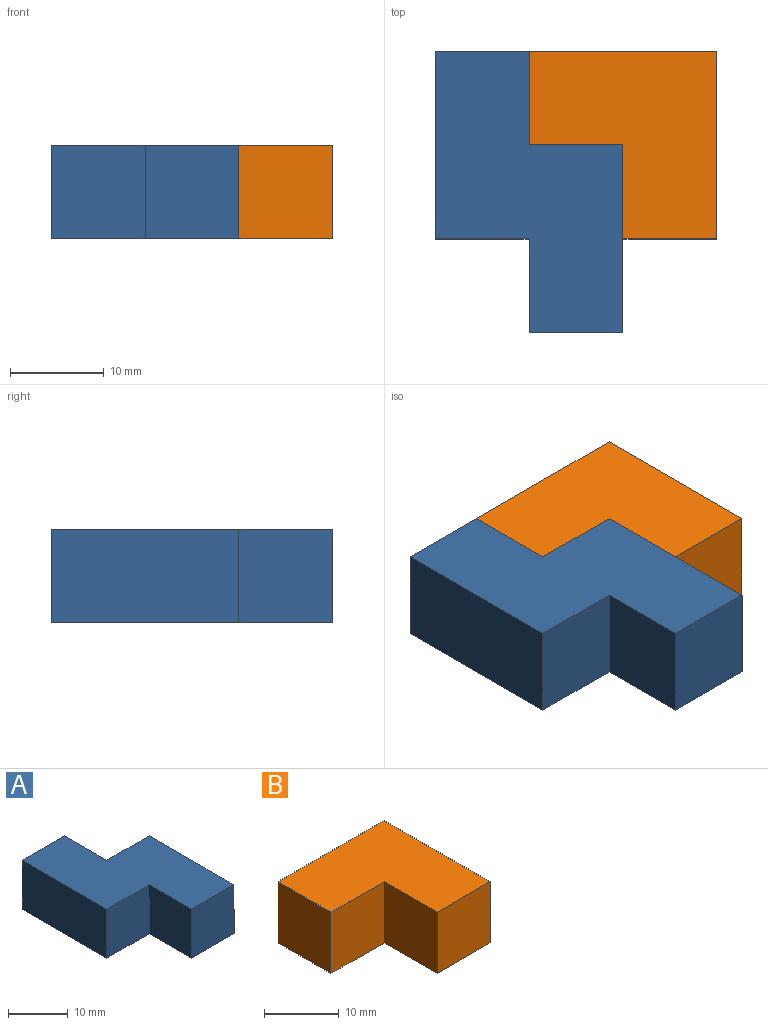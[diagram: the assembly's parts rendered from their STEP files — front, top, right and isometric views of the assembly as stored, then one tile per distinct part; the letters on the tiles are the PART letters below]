
ASSEMBLY  parts=2 mates=1
PART A: 10 faces, bbox 20x30x10 mm
  f0: plane 10x10mm, normal (0,1,0), area 100mm2, adj f2,f3,f4,f8
  f1: plane 10x10mm, normal (-1,0,0), area 100mm2, adj f2,f4,f5,f6
  f2: plane 30x20mm, normal (0,0,-1), area 400mm2, adj f0,f1,f3,f5,f6,f7,f8,f9
  f3: plane 20x10mm, normal (1,0,0), area 200mm2, adj f0,f2,f4,f5
  f4: plane 30x20mm, normal (0,0,1), area 400mm2, adj f0,f1,f3,f5,f6,f7,f8,f9
  f5: plane 10x10mm, normal (0,-1,0), area 100mm2, adj f1,f2,f3,f4
  f6: plane 10x10mm, normal (0,-1,0), area 100mm2, adj f1,f2,f4,f7
  f7: plane 20x10mm, normal (-1,0,0), area 200mm2, adj f2,f4,f6,f9
  f8: plane 10x10mm, normal (1,0,0), area 100mm2, adj f0,f2,f4,f9
  f9: plane 10x10mm, normal (0,1,0), area 100mm2, adj f2,f4,f7,f8
PART B: 8 faces, bbox 20x20x10 mm
  f0: plane 20x20mm, normal (0,0,1), area 300mm2, adj f1,f3,f4,f5,f6,f7
  f1: plane 10x10mm, normal (-1,0,0), area 100mm2, adj f0,f2,f3,f4
  f2: plane 20x20mm, normal (0,0,-1), area 300mm2, adj f1,f3,f4,f5,f6,f7
  f3: plane 10x10mm, normal (0,-1,0), area 100mm2, adj f0,f1,f2,f6
  f4: plane 20x10mm, normal (0,1,0), area 200mm2, adj f0,f1,f2,f5
  f5: plane 20x10mm, normal (1,0,0), area 200mm2, adj f0,f2,f4,f7
  f6: plane 10x10mm, normal (-1,0,0), area 100mm2, adj f0,f2,f3,f7
  f7: plane 10x10mm, normal (0,-1,0), area 100mm2, adj f0,f2,f5,f6
PLACE A t=(-14.29,-2.31,3.91)mm
PLACE B t=(28.88,7.69,-51.96)mm
MATE fastened A.f8 <-> B.f1  axis (1,0,0) through (-24.29,2.69,8.91)mm
